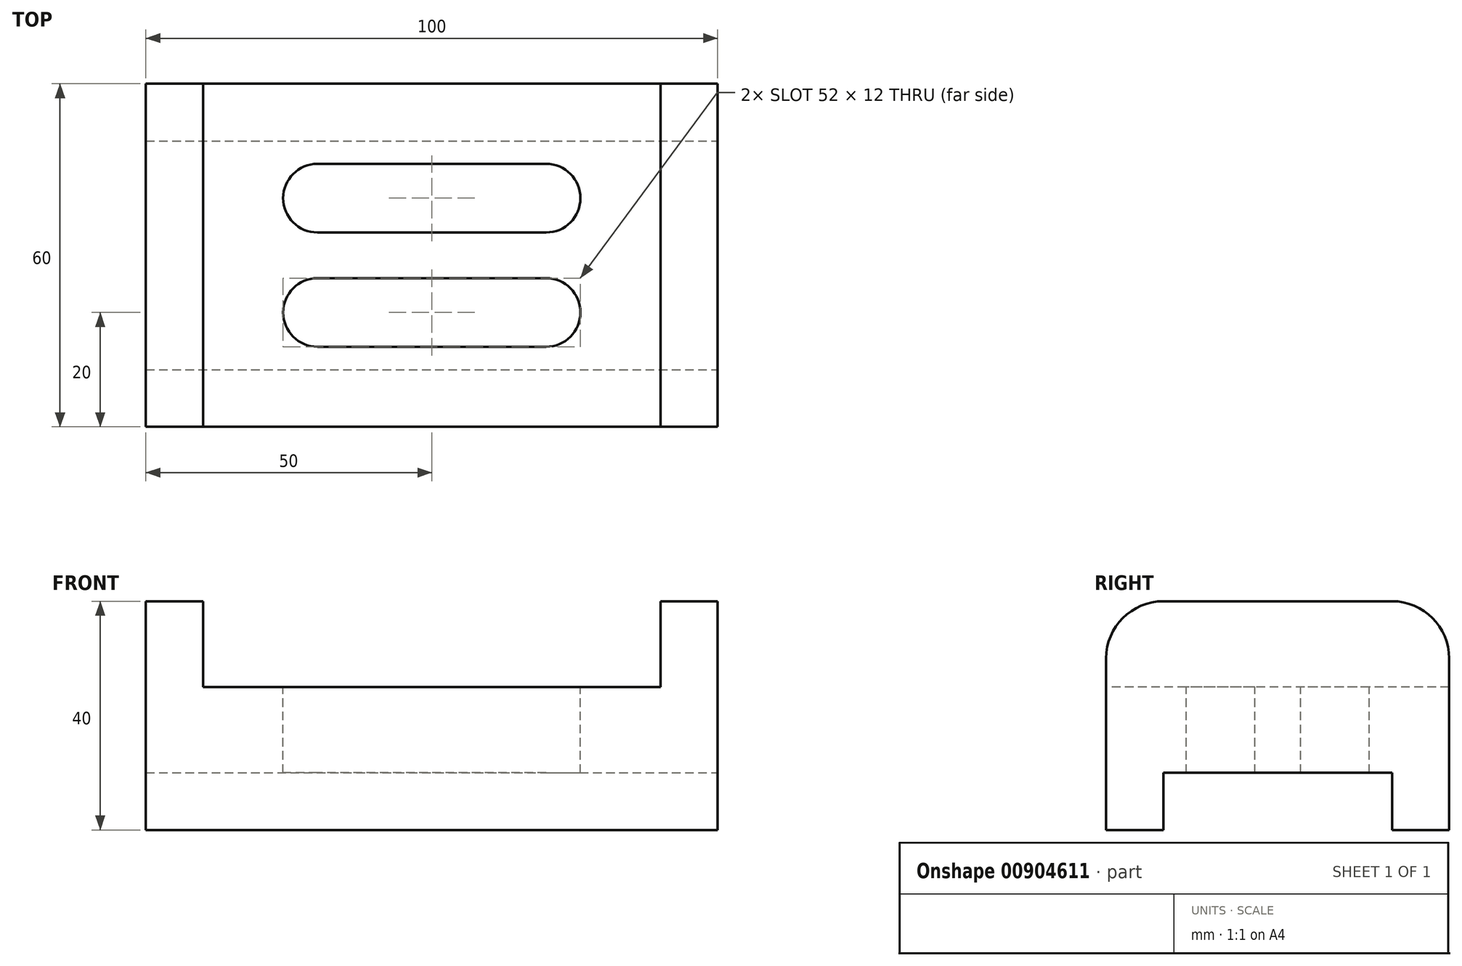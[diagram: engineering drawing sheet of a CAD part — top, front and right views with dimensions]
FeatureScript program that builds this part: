
annotation { "Feature Type Name" : "Feature", "Feature Type Description" : "" }
export const myFeature = defineFeature(function(context is Context, id is Id, definition is map)
    precondition{}
    {
        {
            var Q0;
            Q0=qCreatedBy(makeId("Top.planeOp"),FACE);
            var sketch = newSketch(context, id + "F0", { "sketchPlane" : qUnion([Q0])});
            skLineSegment(sketch, "E0", {"start": v(-60.6, 0) * mm, "end": v(67.85, 0) * mm, "construction": true});
            skLineSegment(sketch, "E1", {"start": v(0, 59.8) * mm, "end": v(0, -61) * mm, "construction": true});
            skLineSegment(sketch, "E2.bottom", {"start": v(50, -30) * mm, "end": v(-50, -30) * mm});
            skLineSegment(sketch, "E2.top", {"start": v(50, 30) * mm, "end": v(-50, 30) * mm});
            skLineSegment(sketch, "E2.left", {"start": v(50, -30) * mm, "end": v(50, 30) * mm});
            skLineSegment(sketch, "E2.right", {"start": v(-50, -30) * mm, "end": v(-50, 30) * mm});
            skPoint(sketch, "E2.middle", {"position": v(0, 0) * mm});
            skLineSegment(sketch, "E3.0", {"start": v(-60.6, 10) * mm, "end": v(67.85, 10) * mm, "construction": true});
            skLineSegment(sketch, "E4.MirrorCS", {"start": v(-60.6, -10) * mm, "end": v(67.85, -10) * mm, "construction": true});
            skLineSegment(sketch, "E5.0", {"start": v(20, -20) * mm, "end": v(20, 20) * mm, "construction": true});
            skLineSegment(sketch, "E6.0", {"start": v(-20, -20) * mm, "end": v(-20, 20) * mm, "construction": true});
            skSolve(sketch);
        }
        {
            var Q0;
            Q0=makeQuery(id+"F0.imprint","IMPRINT",FACE,{"disambiguationData":[TD([[makeQuery(id+"F0.imprint","IMPRINT",EDGE,{"derivedFrom":sQuery(id+"F0.wireOp",EDGE,"E2.bottom")}),-1.0]])]});
            extrude(context, id + "F1", {"entities" : qUnion([Q0]), "depth" : 40 * mm, "offsetDistance" : 25 * mm});
        }
        {
            var Q0;
            Q0=makeQuery(id+"F1.opExtrude","SWEPT_FACE",FACE,{"disambiguationData":[OSD([sQuery(id+"F0.wireOp",EDGE,"E2.left")])]});
            var sketch = newSketch(context, id + "F2", { "sketchPlane" : qUnion([Q0])});
            skLineSegment(sketch, "E7", {"start": v(0, 0) * mm, "end": v(0, 50) * mm, "construction": true});
            skLineSegment(sketch, "E8.bottom", {"start": v(-20, 0) * mm, "end": v(20, 0) * mm});
            skLineSegment(sketch, "E8.top", {"start": v(-20, 10) * mm, "end": v(20, 10) * mm});
            skLineSegment(sketch, "E8.left", {"start": v(-20, 0) * mm, "end": v(-20, 10) * mm});
            skLineSegment(sketch, "E8.right", {"start": v(20, 0) * mm, "end": v(20, 10) * mm});
            skSolve(sketch);
        }
        {
            var Q0;
            Q0=makeQuery(id+"F2.imprint","IMPRINT",FACE,{"disambiguationData":[TD([[makeQuery(id+"F2.imprint","IMPRINT",EDGE,{"derivedFrom":sQuery(id+"F2.wireOp",EDGE,"E8.bottom")}),1.0]])]});
            extrude(context, id + "F3", {"entities" : qUnion([Q0]), "operationType" : NewBodyOperationType.REMOVE, "endBound" : BoundingType.THROUGH_ALL, "oppositeDirection" : true, "depth" : 25 * mm, "offsetDistance" : 25 * mm});
        }
        {
            var Q0;
            Q0=makeQuery(id+"F1.opExtrude","CAP_FACE",FACE,{"disambiguationData":[OSD([sQuery(id+"F0.wireOp",EDGE,"E2.bottom"),sQuery(id+"F0.wireOp",EDGE,"E2.top"),sQuery(id+"F0.wireOp",EDGE,"E2.left"),sQuery(id+"F0.wireOp",EDGE,"E2.right")])],"isStart":false});
            var sketch = newSketch(context, id + "F4", { "sketchPlane" : qUnion([Q0])});
            skLineSegment(sketch, "E9", {"start": v(0, 76.3) * mm, "end": v(0, -76.98) * mm, "construction": true});
            skLineSegment(sketch, "E10.bottom", {"start": v(-40, 30) * mm, "end": v(40, 30) * mm});
            skLineSegment(sketch, "E10.top", {"start": v(-40, -30) * mm, "end": v(40, -30) * mm});
            skLineSegment(sketch, "E10.left", {"start": v(-40, 30) * mm, "end": v(-40, -30) * mm});
            skLineSegment(sketch, "E10.right", {"start": v(40, 30) * mm, "end": v(40, -30) * mm});
            skSolve(sketch);
        }
        {
            var Q0;
            Q0=makeQuery(id+"F4.imprint","IMPRINT",FACE,{"disambiguationData":[TD([[makeQuery(id+"F4.imprint","IMPRINT",EDGE,{"derivedFrom":sQuery(id+"F4.wireOp",EDGE,"E10.bottom")}),1.0]])]});
            extrude(context, id + "F5", {"entities" : qUnion([Q0]), "operationType" : NewBodyOperationType.REMOVE, "oppositeDirection" : true, "depth" : 15 * mm, "offsetDistance" : 25 * mm});
        }
        {
            var Q0;
            Q0=makeQuery(id+"F5.boolean.opBoolean","COPY",FACE,{"derivedFrom":makeQuery(id+"F5.opExtrude","CAP_FACE",FACE,{"disambiguationData":[OSD([sQuery(id+"F4.wireOp",EDGE,"E10.bottom"),sQuery(id+"F4.wireOp",EDGE,"E10.top"),sQuery(id+"F4.wireOp",EDGE,"E10.left"),sQuery(id+"F4.wireOp",EDGE,"E10.right")])],"isStart":false})});
            var sketch = newSketch(context, id + "F6", { "sketchPlane" : qUnion([Q0])});
            skLineSegment(sketch, "E11.0", {"start": v(-20, 16) * mm, "end": v(20, 16) * mm});
            skLineSegment(sketch, "E12.MirrorCS", {"start": v(-20, 4) * mm, "end": v(20, 4) * mm});
            skPoint(sketch, "E13", {"position": v(-20, 10) * mm});
            skArc(sketch, "E14", {"start": v(-20, 16) * mm, "mid": v(-26, 10) * mm, "end": v(-20, 4) * mm});
            skPoint(sketch, "E15.orphan", {"position": v(-60.6, 16) * mm});
            skPoint(sketch, "E16.orphan", {"position": v(-60.6, 4) * mm});
            skArc(sketch, "E17.MirrorCS", {"start": v(20, 16) * mm, "mid": v(26, 10) * mm, "end": v(20, 4) * mm});
            skPoint(sketch, "E18.orphan", {"position": v(67.85, 16) * mm});
            skPoint(sketch, "E19.orphan", {"position": v(67.85, 4) * mm});
            skLineSegment(sketch, "E20.MirrorCS", {"start": v(-20, -4) * mm, "end": v(20, -4) * mm});
            skArc(sketch, "E21.MirrorCS", {"start": v(20, -16) * mm, "mid": v(26, -10) * mm, "end": v(20, -4) * mm});
            skLineSegment(sketch, "E22.MirrorCS", {"start": v(-20, -16) * mm, "end": v(20, -16) * mm});
            skArc(sketch, "E23.MirrorCS", {"start": v(-20, -16) * mm, "mid": v(-26, -10) * mm, "end": v(-20, -4) * mm});
            skSolve(sketch);
        }
        {
            var Q0;
            Q0=makeQuery(id+"F6.imprint","IMPRINT",FACE,{"disambiguationData":[TD([[makeQuery(id+"F6.imprint","IMPRINT",EDGE,{"derivedFrom":sQuery(id+"F6.wireOp",EDGE,"E11.0")}),-1.0]])]});
            var Q1;
            Q1=makeQuery(id+"F6.imprint","IMPRINT",FACE,{"disambiguationData":[TD([[makeQuery(id+"F6.imprint","IMPRINT",EDGE,{"derivedFrom":sQuery(id+"F6.wireOp",EDGE,"E20.MirrorCS")}),-1.0]])]});
            extrude(context, id + "F7", {"entities" : qUnion([Q0, Q1]), "operationType" : NewBodyOperationType.REMOVE, "endBound" : BoundingType.THROUGH_ALL, "oppositeDirection" : true, "depth" : 25 * mm, "offsetDistance" : 25 * mm});
        }
        {
            var Q0;
            {var subQ0=sQuery(id+"F0.wireOp",EDGE,"E2.bottom");var subQ1=sQuery(id+"F0.wireOp",EDGE,"E2.left");Q0=makeQuery(id+"F5.boolean.opBoolean","SPLIT",EDGE,{"disambiguationData":[TD([makeQuery(id+"F1.opExtrude","SWEPT_FACE",FACE,{"disambiguationData":[OSD([subQ1])]})])],"derivedFrom":makeQuery(id+"F1.opExtrude","CAP_EDGE",EDGE,{"disambiguationData":[OSD([subQ0])],"isStart":false})});}
            var Q1;
            {var subQ0=sQuery(id+"F0.wireOp",EDGE,"E2.left");var subQ1=sQuery(id+"F0.wireOp",EDGE,"E2.top");Q1=makeQuery(id+"F5.boolean.opBoolean","SPLIT",EDGE,{"disambiguationData":[TD([makeQuery(id+"F1.opExtrude","SWEPT_FACE",FACE,{"disambiguationData":[OSD([subQ0])]})])],"derivedFrom":makeQuery(id+"F1.opExtrude","CAP_EDGE",EDGE,{"disambiguationData":[OSD([subQ1])],"isStart":false})});}
            var Q2;
            {var subQ0=sQuery(id+"F0.wireOp",EDGE,"E2.right");var subQ1=sQuery(id+"F0.wireOp",EDGE,"E2.top");Q2=makeQuery(id+"F5.boolean.opBoolean","SPLIT",EDGE,{"disambiguationData":[TD([makeQuery(id+"F1.opExtrude","SWEPT_FACE",FACE,{"disambiguationData":[OSD([subQ0])]})])],"derivedFrom":makeQuery(id+"F1.opExtrude","CAP_EDGE",EDGE,{"disambiguationData":[OSD([subQ1])],"isStart":false})});}
            var Q3;
            {var subQ0=sQuery(id+"F0.wireOp",EDGE,"E2.bottom");var subQ1=sQuery(id+"F0.wireOp",EDGE,"E2.right");Q3=makeQuery(id+"F5.boolean.opBoolean","SPLIT",EDGE,{"disambiguationData":[TD([makeQuery(id+"F1.opExtrude","SWEPT_FACE",FACE,{"disambiguationData":[OSD([subQ1])]})])],"derivedFrom":makeQuery(id+"F1.opExtrude","CAP_EDGE",EDGE,{"disambiguationData":[OSD([subQ0])],"isStart":false})});}
            fillet(context, id + "F8", {"entities" : qUnion([Q0, Q1, Q2, Q3]), "radius" : 10 * mm, "tangentPropagation" : true, "allowEdgeOverflow" : false});
        }
    });
